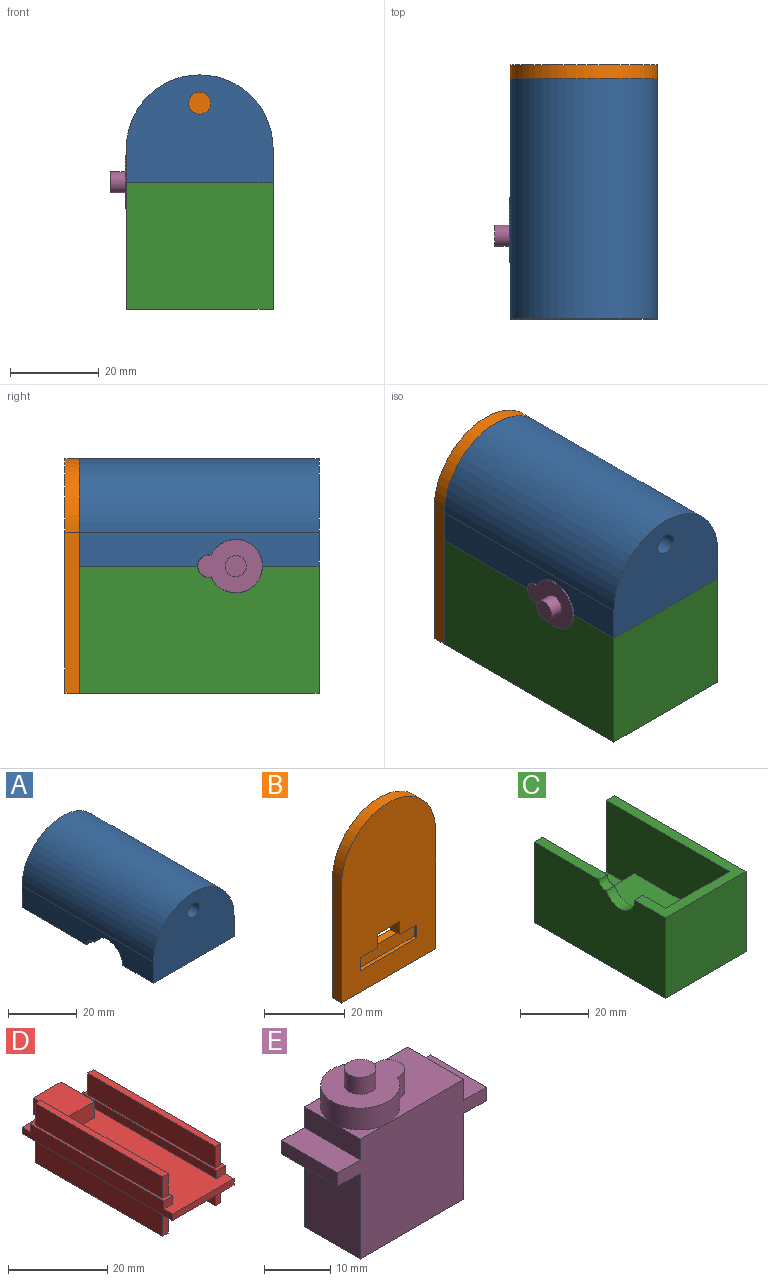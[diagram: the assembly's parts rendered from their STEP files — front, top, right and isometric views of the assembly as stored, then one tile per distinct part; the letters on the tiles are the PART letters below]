
ASSEMBLY  parts=5 mates=9
PART A: 14 faces, bbox 33x54x24.1 mm
  f0: cylinder r=13.08mm len=50.55mm, axis (0,1,0), area 2077.2mm2, adj f2,f6,f7,f8
  f1: plane 53.98x7.62mm, normal (-1,0,0), area 348.2mm2, adj f3,f4,f8,f9,f10,f11,f12
  f2: plane 50.55x7.62mm, normal (1,0,0), area 322.1mm2, adj f0,f3,f7,f8,f9,f10,f11
  f3: plane 53.98x33.02mm, normal (0,0,-1), area 318.3mm2, adj f1,f2,f4,f5,f6,f7,f8,f11
  f4: plane 33.02x24.13mm, normal (0,-1,0), area 660.1mm2, adj f1,f3,f5,f12,f13
  f5: plane 53.98x7.62mm, normal (1,0,0), area 411.3mm2, adj f3,f4,f8,f12
  f6: plane 50.55x7.62mm, normal (-1,0,0), area 385.2mm2, adj f0,f3,f7,f8
  f7: plane 26.16x20.7mm, normal (0,1,0), area 448.5mm2, adj f0,f2,f3,f6,f13
  f8: plane 33.02x24.13mm, normal (0,1,0), area 211.6mm2, adj f0,f1,f2,f3,f5,f6,f9,f12
  f9: plane 26.63x3.43mm, normal (0,0,-1), area 91.3mm2, adj f1,f2,f8,f10
  f10: cylinder r=2.55mm len=3.43mm, axis (-1,0,0), area 15.6mm2, adj f1,f2,f9,f11
  f11: cylinder r=6.05mm len=11.56mm, axis (-1,0,0), area 56.4mm2, adj f1,f2,f3,f10
  f12: cylinder r=16.51mm len=53.98mm, axis (0,1,0), area 2799.6mm2, adj f1,f4,f5,f8
  f13: cylinder r=2.5mm len=5mm, axis (0,-1,0), area 53.9mm2, adj f4,f7
PART B: 16 faces, bbox 33x3.2x52.7 mm
  f0: plane 7.87x2.18mm, normal (0,0,1), area 17.1mm2, adj f2,f4,f9,f15
  f1: plane 52.71x33.02mm, normal (0,-1,0), area 1511.3mm2, adj f2,f3,f4,f5,f6,f7,f8,f10
  f2: plane 4.06x3.18mm, normal (1,0,0), area 12.9mm2, adj f0,f1,f3,f9,f11
  f3: plane 7.87x3.18mm, normal (0,0,-1), area 25mm2, adj f1,f2,f4,f9
  f4: plane 4.06x3.18mm, normal (-1,0,0), area 12.9mm2, adj f0,f1,f3,f9,f10
  f5: cylinder r=16.51mm len=33.02mm, axis (0,1,0), area 164.7mm2, adj f1,f6,f8,f9
  f6: plane 36.2x3.18mm, normal (-1,0,0), area 114.9mm2, adj f1,f5,f7,f9
  f7: plane 33.02x3.18mm, normal (0,0,-1), area 104.8mm2, adj f1,f6,f8,f9
  f8: plane 36.2x3.18mm, normal (1,0,0), area 114.9mm2, adj f1,f5,f7,f9
  f9: plane 52.71x33.02mm, normal (0,1,0), area 1591.3mm2, adj f0,f2,f3,f4,f5,f6,f7,f8
  f10: plane 6.06x1mm, normal (0,0,-1), area 6.1mm2, adj f1,f4,f14,f15
  f11: plane 6.06x1mm, normal (0,0,-1), area 6.1mm2, adj f1,f2,f12,f15
  f12: plane 4x1mm, normal (1,0,0), area 4mm2, adj f1,f11,f13,f15
  f13: plane 20x1mm, normal (0,0,1), area 20mm2, adj f1,f12,f14,f15
  f14: plane 4x1mm, normal (-1,0,0), area 4mm2, adj f1,f10,f13,f15
  f15: plane 20x4mm, normal (0,-1,0), area 80mm2, adj f0,f10,f11,f12,f13,f14
PART C: 18 faces, bbox 33x54x28.6 mm
  f0: plane 50.55x25.4mm, normal (1,0,0), area 1170mm2, adj f1,f3,f5,f9,f10,f11,f12,f13
  f1: plane 53.98x33.02mm, normal (0,0,1), area 318.3mm2, adj f0,f2,f4,f5,f6,f8,f9,f12
  f2: plane 53.98x28.58mm, normal (-1,0,0), area 1479.3mm2, adj f1,f5,f6,f7,f10,f11,f12
  f3: plane 50.55x26.16mm, normal (0,0,1), area 1322.4mm2, adj f0,f5,f8,f9
  f4: plane 53.98x28.58mm, normal (1,0,0), area 1542.3mm2, adj f1,f5,f6,f7
  f5: plane 33.02x28.58mm, normal (0,1,0), area 279mm2, adj f0,f1,f2,f3,f4,f7,f8,f10
  f6: plane 33.02x28.58mm, normal (0,-1,0), area 943.5mm2, adj f1,f2,f4,f7
  f7: plane 53.98x33.02mm, normal (0,0,-1), area 1782.3mm2, adj f2,f4,f5,f6
  f8: plane 50.55x25.4mm, normal (-1,0,0), area 1283.9mm2, adj f1,f3,f5,f9
  f9: plane 26.16x25.4mm, normal (0,1,0), area 664.5mm2, adj f0,f1,f3,f8
  f10: plane 26.63x3.43mm, normal (0,0,1), area 91.3mm2, adj f0,f2,f5,f11
  f11: cylinder r=2.55mm len=3.43mm, axis (-1,0,0), area 15.6mm2, adj f0,f2,f10,f12
  f12: cylinder r=6.05mm len=11.56mm, axis (-1,0,0), area 56.4mm2, adj f0,f1,f2,f11
  f13: plane 12.7x2.5mm, normal (0,-1,0), area 31.8mm2, adj f0,f14,f16,f17
  f14: plane 20.32x12.7mm, normal (0,0,-1), area 258.1mm2, adj f0,f13,f15,f17
  f15: plane 12.7x2.5mm, normal (0,1,0), area 31.8mm2, adj f0,f14,f16,f17
  f16: plane 20.32x12.7mm, normal (0,0,1), area 258.1mm2, adj f0,f13,f15,f17
  f17: plane 20.32x2.5mm, normal (1,0,0), area 50.8mm2, adj f13,f14,f15,f16
PART D: 40 faces, bbox 17.5x44.5x14.6 mm
  f0: plane 42.86x17.46mm, normal (0,0,1), area 496.2mm2, adj f1,f2,f3,f4,f7,f9,f10,f12
  f1: plane 42.86x3.59mm, normal (1,0,0), area 143.8mm2, adj f0,f2,f4,f5,f16,f18,f19
  f2: plane 17.46x1.59mm, normal (0,1,0), area 27.7mm2, adj f0,f1,f3,f5,f6
  f3: plane 42.86x3.59mm, normal (-1,0,0), area 143.8mm2, adj f0,f2,f4,f5,f12,f13,f15
  f4: plane 17.46x1.59mm, normal (0,-1,0), area 27.7mm2, adj f0,f1,f3,f5
  f5: plane 42.86x17.46mm, normal (0,0,-1), area 633.3mm2, adj f1,f2,f3,f4,f25,f26,f27,f28
  f6: plane 7.94x1.59mm, normal (0,0,-1), area 12.6mm2, adj f2,f7,f8,f9
  f7: plane 9.53x4mm, normal (1,0,0), area 38.1mm2, adj f0,f6,f8,f10,f11
  f8: plane 7.94x4mm, normal (0,1,0), area 31.8mm2, adj f6,f7,f9,f11
  f9: plane 9.53x4mm, normal (-1,0,0), area 38.1mm2, adj f0,f6,f8,f10,f11
  f10: plane 7.94x4mm, normal (0,-1,0), area 31.8mm2, adj f0,f7,f9,f11
  f11: plane 9.53x7.94mm, normal (0,0,1), area 75.6mm2, adj f7,f8,f9,f10
  f12: plane 2.5x2mm, normal (0,1,0), area 5mm2, adj f0,f3,f14,f15
  f13: plane 2.5x2mm, normal (0,-1,0), area 5mm2, adj f0,f3,f14,f15
  f14: plane 37.86x2mm, normal (1,0,0), area 75.7mm2, adj f0,f12,f13,f15
  f15: plane 37.86x2.5mm, normal (0,0,1), area 37.1mm2, adj f3,f12,f13,f14,f21,f22,f23,f24
  f16: plane 2.5x2mm, normal (0,1,0), area 5mm2, adj f0,f1,f17,f19
  f17: plane 37.86x2mm, normal (-1,0,0), area 75.7mm2, adj f0,f16,f18,f19
  f18: plane 2.5x2mm, normal (0,-1,0), area 5mm2, adj f0,f1,f17,f19
  f19: plane 37.86x2.5mm, normal (0,0,1), area 37.1mm2, adj f1,f16,f17,f18,f31,f32,f33,f34
  f20: plane 36.28x1.59mm, normal (0,0,1), area 57.6mm2, adj f21,f22,f23,f24
  f21: plane 5.3x1.59mm, normal (0,-1,0), area 8.4mm2, adj f15,f20,f22,f24
  f22: plane 36.28x5.3mm, normal (-1,0,0), area 192.3mm2, adj f15,f20,f21,f23
  f23: plane 5.3x1.59mm, normal (0,1,0), area 8.4mm2, adj f15,f20,f22,f24
  f24: plane 36.28x5.3mm, normal (1,0,0), area 192.3mm2, adj f15,f20,f21,f23
  f25: plane 36.28x5.72mm, normal (1,0,0), area 207.3mm2, adj f5,f26,f28,f29
  f26: plane 5.72x1.59mm, normal (0,1,0), area 9.1mm2, adj f5,f25,f27,f29
  f27: plane 36.28x5.72mm, normal (-1,0,0), area 207.3mm2, adj f5,f26,f28,f29
  f28: plane 5.72x1.59mm, normal (0,-1,0), area 9.1mm2, adj f5,f25,f27,f29
  f29: plane 36.28x1.59mm, normal (0,0,-1), area 57.6mm2, adj f25,f26,f27,f28
  f30: plane 36.28x1.59mm, normal (0,0,1), area 57.6mm2, adj f31,f32,f33,f34
  f31: plane 36.28x5.3mm, normal (1,0,0), area 192.3mm2, adj f19,f30,f32,f34
  f32: plane 5.3x1.59mm, normal (0,-1,0), area 8.4mm2, adj f19,f30,f31,f33
  f33: plane 36.28x5.3mm, normal (-1,0,0), area 192.3mm2, adj f19,f30,f32,f34
  f34: plane 5.3x1.59mm, normal (0,1,0), area 8.4mm2, adj f19,f30,f31,f33
  f35: plane 5.72x1.59mm, normal (0,1,0), area 9.1mm2, adj f5,f36,f38,f39
  f36: plane 36.28x5.72mm, normal (-1,0,0), area 207.3mm2, adj f5,f35,f37,f39
  f37: plane 5.72x1.59mm, normal (0,-1,0), area 9.1mm2, adj f5,f36,f38,f39
  f38: plane 36.28x5.72mm, normal (1,0,0), area 207.3mm2, adj f5,f35,f37,f39
  f39: plane 36.28x1.59mm, normal (0,0,-1), area 57.6mm2, adj f35,f36,f37,f38
PART E: 21 faces, bbox 31.8x12x29.4 mm
  f0: plane 16.23x12mm, normal (0,0,1), area 127.5mm2, adj f6,f14,f15,f16,f17
  f1: plane 6x6mm, normal (0,0,1), area 7.7mm2, adj f8,f15,f16
  f2: plane 15.88x12mm, normal (1,0,0), area 190.5mm2, adj f3,f13,f14,f15
  f3: plane 12x4.76mm, normal (0,0,-1), area 57.1mm2, adj f2,f4,f14,f15
  f4: plane 12x2.5mm, normal (1,0,0), area 30mm2, adj f3,f5,f14,f15
  f5: plane 12x4.76mm, normal (0,0,1), area 57.1mm2, adj f4,f6,f14,f15
  f6: plane 12x3.85mm, normal (1,0,0), area 46.2mm2, adj f0,f5,f14,f15
  f7: plane 6x6mm, normal (0,0,1), area 7.7mm2, adj f8,f14,f16
  f8: plane 12x3.85mm, normal (-1,0,0), area 46.2mm2, adj f1,f7,f9,f14,f15
  f9: plane 12x4.76mm, normal (0,0,1), area 57.1mm2, adj f8,f10,f14,f15
  f10: plane 12x2.5mm, normal (-1,0,0), area 30mm2, adj f9,f11,f14,f15
  f11: plane 12x4.76mm, normal (0,0,-1), area 57.1mm2, adj f10,f12,f14,f15
  f12: plane 15.88x12mm, normal (-1,0,0), area 190.5mm2, adj f11,f13,f14,f15
  f13: plane 22.23x12mm, normal (0,0,-1), area 266.7mm2, adj f2,f12,f14,f15
  f14: plane 31.75x22.23mm, normal (0,-1,0), area 517.8mm2, adj f0,f2,f3,f4,f5,f6,f7,f8
  f15: plane 31.75x22.23mm, normal (0,1,0), area 517.8mm2, adj f0,f1,f2,f3,f4,f5,f6,f8
  f16: cylinder r=6mm len=12mm, axis (0,0,-1), area 130.6mm2, adj f0,f1,f7,f17,f18
  f17: cylinder r=2.5mm len=5mm, axis (0,0,-1), area 35.6mm2, adj f0,f16,f18
  f18: plane 14.5x12mm, normal (0,0,1), area 106mm2, adj f16,f17,f19
  f19: cylinder r=2.38mm len=4.76mm, axis (0,0,-1), area 47.5mm2, adj f18,f20
  f20: plane 4.76x4.76mm, normal (0,0,1), area 17.8mm2, adj f19
PLACE A t=(0,0,-25.4)mm
PLACE B t=(0,-20.64,0)mm
PLACE C at identity fixed
PLACE D t=(0.05,5.56,8.89)mm
PLACE E rot(axis=(-0.58,-0.58,0.58),120deg) t=(-1.68,-3.12,22.58)mm
MATE planar A.f4 <-> C.f6  axis (0,-1,0) through (0,-26.99,38.99)mm
MATE revolute C.f12 <-> E.f16  axis (-1,0,0) through (-14.8,-8.24,28.58)mm
MATE planar D.f39 <-> C.f3  axis (0,0,-1) through (7.53,5.56,3.18)mm
MATE planar B.f1 <-> C.f5  axis (0,-1,0) through (0,26.99,25.83)mm
MATE planar D.f2 <-> C.f5  axis (0,1,0) through (0.05,26.99,9.68)mm
MATE planar A.f3 <-> C.f1  axis (0,0,-1) through (6.58,-9.95,28.58)mm
MATE planar B.f7 <-> C.f7  axis (0,0,-1) through (0,28.57,0)mm
MATE parallel C.f3 <-> E.f14  axis (0,0,1) through (0,1.71,3.18)mm
MATE planar A.f1 <-> C.f2  axis (-1,0,0) through (-16.51,1.38,32.63)mm
